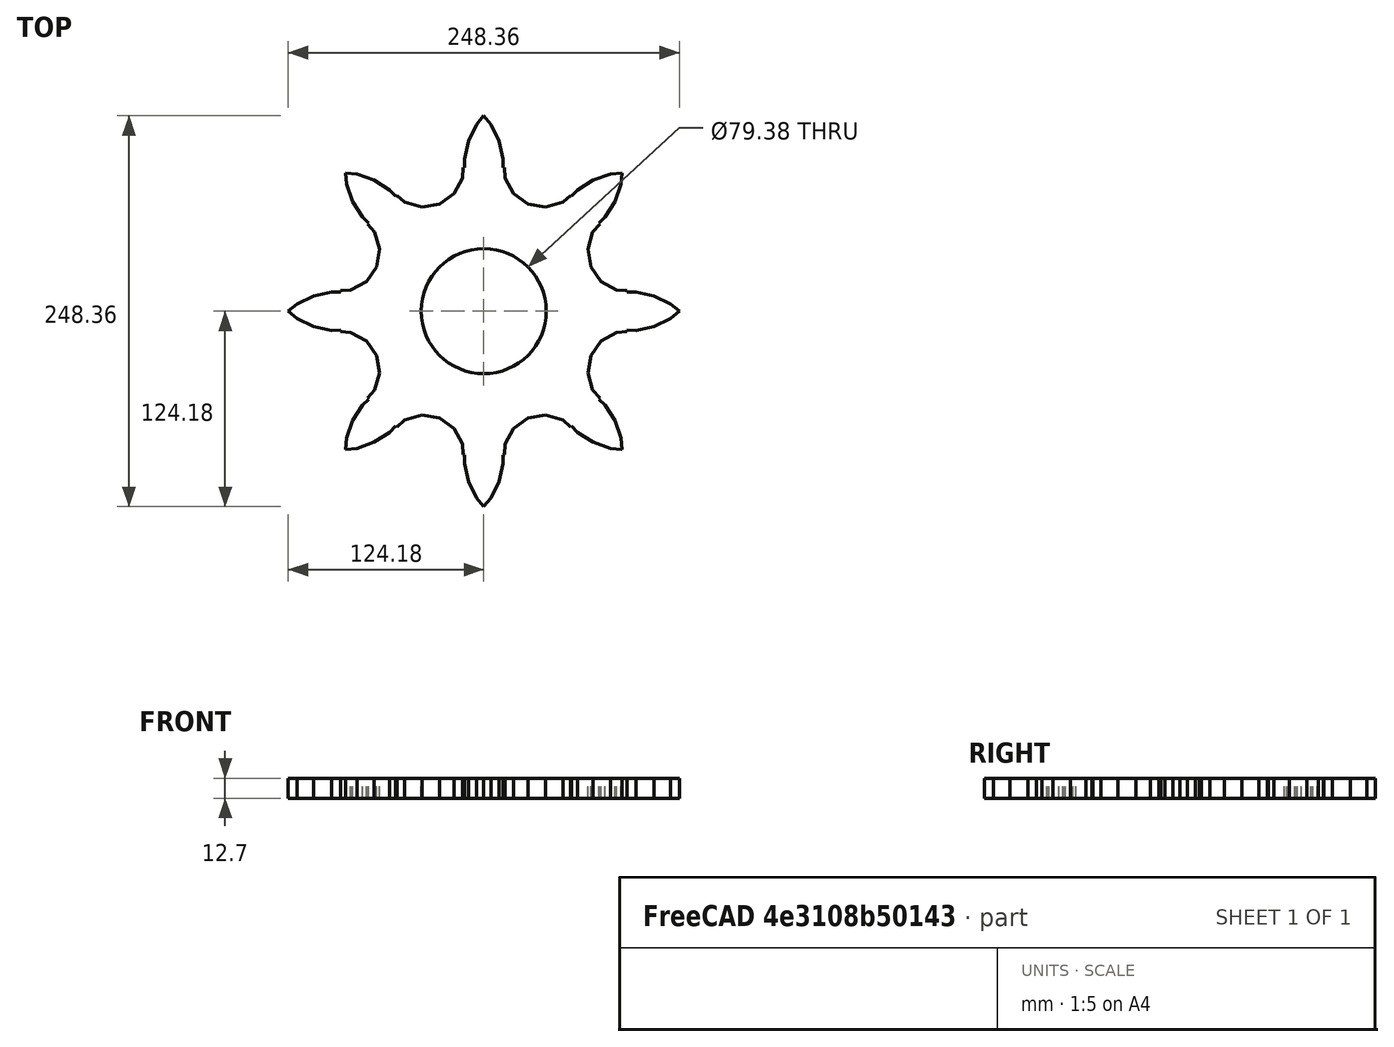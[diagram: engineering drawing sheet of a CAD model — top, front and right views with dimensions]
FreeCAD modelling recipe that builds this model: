
FCSTD DOCUMENT  (FreeCAD 0.16R6712 (Git))
Label: Sprocket
License: All rights reserved
LicenseURL: http://en.wikipedia.org/wiki/All_rights_reserved
objects: Sketcher::SketchObject×1, PartDesign::Pad×1, Part::Feature×1
note: 4 computed .brp shape members not serialized (recipe doc carries the construction recipe); baked Part::Feature solids carry a one-line shape summary decoded from their .brp

FEATURE [Sketcher::SketchObject] Sketch129
  sketch-geometry (129):
    g0: LineSegment StartX=-124.179 StartY=0 StartZ=0 EndX=-118.568 EndY=4.57225 EndZ=0
    g1: LineSegment StartX=-90.9735 StartY=13.09 StartZ=0 EndX=-84.4613 EndY=13.4541 EndZ=0
    g2: LineSegment StartX=-28.1677 StartY=67.9988 StartZ=0 EndX=-18.9337 EndY=74.5528 EndZ=0
    g3: LineSegment StartX=-66.1067 StartY=39.3297 StartZ=0 EndX=-69.2404 EndY=50.2112 EndZ=0
    g4: LineSegment StartX=-18.9337 StartY=74.5528 StartZ=0 EndX=-13.4541 EndY=84.4613 EndZ=0
    g5: LineSegment StartX=4.57225 StartY=118.568 StartZ=0 EndX=9.66978 EndY=108.045 EndZ=0
    g6: LineSegment StartX=55.8281 StartY=72.9651 StartZ=0 EndX=59.696 EndY=76.9523 EndZ=0
    g7: LineSegment StartX=-12.2006 StartY=96.6262 StartZ=0 EndX=-9.66978 EndY=108.045 EndZ=0
    g8: LineSegment StartX=12.2006 StartY=96.6262 StartZ=0 EndX=12.123 EndY=91.3197 EndZ=0
    g9: LineSegment StartX=76.9523 StartY=59.696 StartZ=0 EndX=73.1561 EndY=56.0131 EndZ=0
    g10: LineSegment StartX=83.2317 StartY=69.5568 StartZ=0 EndX=76.9523 EndY=59.696 EndZ=0
    g11: LineSegment StartX=-80.6054 StartY=87.0758 StartZ=0 EndX=-69.5568 EndY=83.2317 EndZ=0
    g12: LineSegment StartX=13.084 StartY=91.1168 StartZ=0 EndX=13.4541 EndY=84.4613 EndZ=0
    g13: LineSegment StartX=-74.5528 StartY=18.9337 StartZ=0 EndX=-67.9988 EndY=28.1677 EndZ=0
    g14: LineSegment StartX=12.123 StartY=91.3197 StartZ=0 EndX=13.084 EndY=91.1168 EndZ=0
    g15: LineSegment StartX=0 StartY=124.179 StartZ=0 EndX=4.57225 EndY=118.568 EndZ=0
    g16: LineSegment StartX=84.4613 StartY=13.4541 StartZ=0 EndX=90.9735 EndY=13.09 EndZ=0
    g17: LineSegment StartX=90.9735 StartY=13.09 StartZ=0 EndX=91.075 EndY=12.1171 EndZ=0
    g18: LineSegment StartX=96.6262 StartY=12.2006 StartZ=0 EndX=108.045 EndY=9.66978 EndZ=0
    g19: LineSegment StartX=91.075 StartY=12.1171 StartZ=0 EndX=96.6262 EndY=12.2006 EndZ=0
    g20: LineSegment StartX=118.568 StartY=4.57225 StartZ=0 EndX=124.179 EndY=0 EndZ=0
    g21: LineSegment StartX=-55.8281 StartY=72.9651 StartZ=0 EndX=-55.0282 EndY=73.544 EndZ=0
    g22: LineSegment StartX=-13.084 StartY=91.1168 StartZ=0 EndX=-12.123 EndY=91.3197 EndZ=0
    g23: LineSegment StartX=-55.0282 StartY=73.544 StartZ=0 EndX=-50.2112 EndY=69.2404 EndZ=0
    g24: LineSegment StartX=-96.6262 StartY=12.2006 StartZ=0 EndX=-91.075 EndY=12.1171 EndZ=0
    g25: LineSegment StartX=50.2112 StartY=69.2404 StartZ=0 EndX=55.0282 EndY=73.544 EndZ=0
    g26: LineSegment StartX=13.4541 StartY=84.4613 StartZ=0 EndX=18.9337 EndY=74.5528 EndZ=0
    g27: LineSegment StartX=39.3297 StartY=66.1067 StartZ=0 EndX=50.2112 EndY=69.2404 EndZ=0
    g28: LineSegment StartX=18.9337 StartY=74.5528 StartZ=0 EndX=28.1677 EndY=67.9988 EndZ=0
    g29: LineSegment StartX=28.1677 StartY=67.9988 StartZ=0 EndX=39.3297 EndY=66.1067 EndZ=0
    g30: LineSegment StartX=-87.81 StartY=87.81 StartZ=0 EndX=-80.6054 EndY=87.0758 EndZ=0
    g31: LineSegment StartX=-108.045 StartY=9.66978 StartZ=0 EndX=-96.6262 EndY=12.2006 EndZ=0
    g32: LineSegment StartX=-4.57225 StartY=118.568 StartZ=0 EndX=0 EndY=124.179 EndZ=0
    g33: LineSegment StartX=9.66978 StartY=108.045 StartZ=0 EndX=12.2006 EndY=96.6262 EndZ=0
    g34: LineSegment StartX=-13.4541 StartY=84.4613 StartZ=0 EndX=-13.084 EndY=91.1168 EndZ=0
    g35: LineSegment StartX=-118.568 StartY=4.57225 StartZ=0 EndX=-108.045 EndY=9.66978 EndZ=0
    g36: LineSegment StartX=-83.2317 StartY=69.5568 StartZ=0 EndX=-87.0758 EndY=80.6054 EndZ=0
    g37: LineSegment StartX=73.1561 StartY=56.0131 StartZ=0 EndX=73.7947 EndY=55.3028 EndZ=0
    g38: LineSegment StartX=73.7947 StartY=55.3028 StartZ=0 EndX=69.2404 EndY=50.2112 EndZ=0
    g39: LineSegment StartX=-76.9523 StartY=59.696 StartZ=0 EndX=-83.2317 EndY=69.5568 EndZ=0
    g40: LineSegment StartX=-91.075 StartY=12.1171 StartZ=0 EndX=-90.9735 EndY=13.09 EndZ=0
    g41: LineSegment StartX=59.696 StartY=76.9523 StartZ=0 EndX=69.5568 EndY=83.2317 EndZ=0
    g42: LineSegment StartX=69.5568 StartY=83.2317 StartZ=0 EndX=80.6054 EndY=87.0758 EndZ=0
    g43: LineSegment StartX=80.6054 StartY=87.0758 StartZ=0 EndX=87.81 EndY=87.81 EndZ=0
    g44: LineSegment StartX=-39.3297 StartY=66.1067 StartZ=0 EndX=-28.1677 EndY=67.9988 EndZ=0
    g45: LineSegment StartX=55.0282 StartY=73.544 StartZ=0 EndX=55.8281 EndY=72.9651 EndZ=0
    g46: LineSegment StartX=-84.4613 StartY=13.4541 StartZ=0 EndX=-74.5528 EndY=18.9337 EndZ=0
    g47: LineSegment StartX=-59.696 StartY=76.9523 StartZ=0 EndX=-55.8281 EndY=72.9651 EndZ=0
    g48: LineSegment StartX=87.81 StartY=87.81 StartZ=0 EndX=87.0758 EndY=80.6054 EndZ=0
    g49: LineSegment StartX=87.0758 StartY=80.6054 StartZ=0 EndX=83.2317 EndY=69.5568 EndZ=0
    g50: LineSegment StartX=-9.66978 StartY=108.045 StartZ=0 EndX=-4.57225 EndY=118.568 EndZ=0
    g51: LineSegment StartX=-87.0758 StartY=80.6054 StartZ=0 EndX=-87.81 EndY=87.81 EndZ=0
    g52: LineSegment StartX=-12.123 StartY=91.3197 StartZ=0 EndX=-12.2006 EndY=96.6262 EndZ=0
    g53: LineSegment StartX=91.075 StartY=-12.1171 StartZ=0 EndX=90.9735 EndY=-13.09 EndZ=0
    g54: LineSegment StartX=108.045 StartY=9.66978 StartZ=0 EndX=118.568 EndY=4.57225 EndZ=0
    g55: LineSegment StartX=118.568 StartY=-4.57225 StartZ=0 EndX=108.045 EndY=-9.66978 EndZ=0
    g56: LineSegment StartX=124.179 StartY=0 StartZ=0 EndX=118.568 EndY=-4.57225 EndZ=0
    g57: LineSegment StartX=108.045 StartY=-9.66978 StartZ=0 EndX=96.6262 EndY=-12.2006 EndZ=0
    g58: LineSegment StartX=-73.7947 StartY=55.3028 StartZ=0 EndX=-73.1561 EndY=56.0131 EndZ=0
    g59: LineSegment StartX=69.2404 StartY=50.2112 StartZ=0 EndX=66.1067 EndY=39.3297 EndZ=0
    g60: LineSegment StartX=66.1067 StartY=39.3297 StartZ=0 EndX=67.9988 EndY=28.1677 EndZ=0
    g61: LineSegment StartX=67.9988 StartY=28.1677 StartZ=0 EndX=74.5528 EndY=18.9337 EndZ=0
    g62: LineSegment StartX=74.5528 StartY=18.9337 StartZ=0 EndX=84.4613 EndY=13.4541 EndZ=0
    g63: LineSegment StartX=-50.2112 StartY=69.2404 StartZ=0 EndX=-39.3297 EndY=66.1067 EndZ=0
    g64: LineSegment StartX=-67.9988 StartY=28.1677 StartZ=0 EndX=-66.1067 EndY=39.3297 EndZ=0
    g65: LineSegment StartX=-69.2404 StartY=50.2112 StartZ=0 EndX=-73.7947 EndY=55.3028 EndZ=0
    g66: LineSegment StartX=-69.5568 StartY=83.2317 StartZ=0 EndX=-59.696 EndY=76.9523 EndZ=0
    g67: LineSegment StartX=96.6262 StartY=-12.2006 StartZ=0 EndX=91.075 EndY=-12.1171 EndZ=0
    g68: LineSegment StartX=67.9988 StartY=-28.1677 StartZ=0 EndX=66.1067 EndY=-39.3297 EndZ=0
    g69: LineSegment StartX=90.9735 StartY=-13.09 StartZ=0 EndX=84.4613 EndY=-13.4541 EndZ=0
    g70: LineSegment StartX=84.4613 StartY=-13.4541 StartZ=0 EndX=74.5528 EndY=-18.9337 EndZ=0
    g71: LineSegment StartX=66.1067 StartY=-39.3297 StartZ=0 EndX=69.2404 EndY=-50.2112 EndZ=0
    g72: LineSegment StartX=74.5528 StartY=-18.9337 StartZ=0 EndX=67.9988 EndY=-28.1677 EndZ=0
    g73: LineSegment StartX=-73.1561 StartY=56.0131 StartZ=0 EndX=-76.9523 EndY=59.696 EndZ=0
    g74: LineSegment StartX=69.2404 StartY=-50.2112 StartZ=0 EndX=73.7947 EndY=-55.3028 EndZ=0
    g75: LineSegment StartX=73.7947 StartY=-55.3028 StartZ=0 EndX=73.1561 EndY=-56.0131 EndZ=0
    g76: LineSegment StartX=73.1561 StartY=-56.0131 StartZ=0 EndX=76.9523 EndY=-59.696 EndZ=0
    g77: LineSegment StartX=83.2317 StartY=-69.5568 StartZ=0 EndX=87.0758 EndY=-80.6054 EndZ=0
    g78: LineSegment StartX=87.0758 StartY=-80.6054 StartZ=0 EndX=87.81 EndY=-87.81 EndZ=0
    g79: LineSegment StartX=76.9523 StartY=-59.696 StartZ=0 EndX=83.2317 EndY=-69.5568 EndZ=0
    g80: LineSegment StartX=87.81 StartY=-87.81 StartZ=0 EndX=80.6054 EndY=-87.0758 EndZ=0
    g81: LineSegment StartX=80.6054 StartY=-87.0758 StartZ=0 EndX=69.5568 EndY=-83.2317 EndZ=0
    g82: LineSegment StartX=69.5568 StartY=-83.2317 StartZ=0 EndX=59.696 EndY=-76.9523 EndZ=0
    g83: LineSegment StartX=59.696 StartY=-76.9523 StartZ=0 EndX=55.8281 EndY=-72.9651 EndZ=0
    g84: LineSegment StartX=50.2112 StartY=-69.2404 StartZ=0 EndX=39.3297 EndY=-66.1067 EndZ=0
    g85: LineSegment StartX=55.8281 StartY=-72.9651 StartZ=0 EndX=55.0282 EndY=-73.544 EndZ=0
    g86: LineSegment StartX=55.0282 StartY=-73.544 StartZ=0 EndX=50.2112 EndY=-69.2404 EndZ=0
    g87: LineSegment StartX=39.3297 StartY=-66.1067 StartZ=0 EndX=28.1677 EndY=-67.9988 EndZ=0
    g88: LineSegment StartX=28.1677 StartY=-67.9988 StartZ=0 EndX=18.9337 EndY=-74.5528 EndZ=0
    g89: LineSegment StartX=13.4541 StartY=-84.4613 StartZ=0 EndX=13.084 EndY=-91.1168 EndZ=0
    g90: LineSegment StartX=18.9337 StartY=-74.5528 StartZ=0 EndX=13.4541 EndY=-84.4613 EndZ=0
    g91: LineSegment StartX=13.084 StartY=-91.1168 StartZ=0 EndX=12.123 EndY=-91.3197 EndZ=0
    g92: LineSegment StartX=12.123 StartY=-91.3197 StartZ=0 EndX=12.2006 EndY=-96.6262 EndZ=0
    g93: LineSegment StartX=12.2006 StartY=-96.6262 StartZ=0 EndX=9.66978 EndY=-108.045 EndZ=0
    g94: LineSegment StartX=9.66978 StartY=-108.045 StartZ=0 EndX=4.57225 EndY=-118.568 EndZ=0
    g95: LineSegment StartX=4.57225 StartY=-118.568 StartZ=0 EndX=0 EndY=-124.179 EndZ=0
    g96: LineSegment StartX=-9.66978 StartY=-108.045 StartZ=0 EndX=-12.2006 EndY=-96.6262 EndZ=0
    g97: LineSegment StartX=0 StartY=-124.179 StartZ=0 EndX=-4.57225 EndY=-118.568 EndZ=0
    g98: LineSegment StartX=-4.57225 StartY=-118.568 StartZ=0 EndX=-9.66978 EndY=-108.045 EndZ=0
    g99: LineSegment StartX=-12.2006 StartY=-96.6262 StartZ=0 EndX=-12.123 EndY=-91.3197 EndZ=0
    g100: LineSegment StartX=-12.123 StartY=-91.3197 StartZ=0 EndX=-13.084 EndY=-91.1168 EndZ=0
    g101: LineSegment StartX=-13.084 StartY=-91.1168 StartZ=0 EndX=-13.4541 EndY=-84.4613 EndZ=0
    g102: LineSegment StartX=-13.4541 StartY=-84.4613 StartZ=0 EndX=-18.9337 EndY=-74.5528 EndZ=0
    g103: LineSegment StartX=-18.9337 StartY=-74.5528 StartZ=0 EndX=-28.1677 EndY=-67.9988 EndZ=0
    g104: LineSegment StartX=-28.1677 StartY=-67.9988 StartZ=0 EndX=-39.3297 EndY=-66.1067 EndZ=0
    g105: LineSegment StartX=-39.3297 StartY=-66.1067 StartZ=0 EndX=-50.2112 EndY=-69.2404 EndZ=0
    g106: LineSegment StartX=-50.2112 StartY=-69.2404 StartZ=0 EndX=-55.0282 EndY=-73.544 EndZ=0
    g107: LineSegment StartX=-55.0282 StartY=-73.544 StartZ=0 EndX=-55.8281 EndY=-72.9651 EndZ=0
    g108: LineSegment StartX=-55.8281 StartY=-72.9651 StartZ=0 EndX=-59.696 EndY=-76.9523 EndZ=0
    g109: LineSegment StartX=-69.5568 StartY=-83.2317 StartZ=0 EndX=-80.6054 EndY=-87.0758 EndZ=0
    g110: LineSegment StartX=-59.696 StartY=-76.9523 StartZ=0 EndX=-69.5568 EndY=-83.2317 EndZ=0
    g111: LineSegment StartX=-80.6054 StartY=-87.0758 StartZ=0 EndX=-87.81 EndY=-87.81 EndZ=0
    g112: LineSegment StartX=-87.0758 StartY=-80.6054 StartZ=0 EndX=-83.2317 EndY=-69.5568 EndZ=0
    g113: LineSegment StartX=-87.81 StartY=-87.81 StartZ=0 EndX=-87.0758 EndY=-80.6054 EndZ=0
    g114: LineSegment StartX=-83.2317 StartY=-69.5568 StartZ=0 EndX=-76.9523 EndY=-59.696 EndZ=0
    g115: LineSegment StartX=-73.1561 StartY=-56.0131 StartZ=0 EndX=-73.7947 EndY=-55.3028 EndZ=0
    g116: LineSegment StartX=-76.9523 StartY=-59.696 StartZ=0 EndX=-73.1561 EndY=-56.0131 EndZ=0
    g117: LineSegment StartX=-73.7947 StartY=-55.3028 StartZ=0 EndX=-69.2404 EndY=-50.2112 EndZ=0
    g118: LineSegment StartX=-66.1067 StartY=-39.3297 StartZ=0 EndX=-67.9988 EndY=-28.1677 EndZ=0
    g119: LineSegment StartX=-69.2404 StartY=-50.2112 StartZ=0 EndX=-66.1067 EndY=-39.3297 EndZ=0
    g120: LineSegment StartX=-67.9988 StartY=-28.1677 StartZ=0 EndX=-74.5528 EndY=-18.9337 EndZ=0
    g121: LineSegment StartX=-74.5528 StartY=-18.9337 StartZ=0 EndX=-84.4613 EndY=-13.4541 EndZ=0
    g122: LineSegment StartX=-84.4613 StartY=-13.4541 StartZ=0 EndX=-90.9735 EndY=-13.09 EndZ=0
    g123: LineSegment StartX=-90.9735 StartY=-13.09 StartZ=0 EndX=-91.075 EndY=-12.1171 EndZ=0
    g124: LineSegment StartX=-91.075 StartY=-12.1171 StartZ=0 EndX=-96.6262 EndY=-12.2006 EndZ=0
    g125: LineSegment StartX=-96.6262 StartY=-12.2006 StartZ=0 EndX=-108.045 EndY=-9.66978 EndZ=0
    g126: LineSegment StartX=-108.045 StartY=-9.66978 StartZ=0 EndX=-118.568 EndY=-4.57225 EndZ=0
    g127: Circle CenterX=0 CenterY=0 CenterZ=0 NormalX=0 NormalY=0 NormalZ=-1 Radius=39.6875
    g128: LineSegment StartX=-118.568 StartY=-4.57225 StartZ=0 EndX=-124.179 EndY=0 EndZ=0
FEATURE [PartDesign::Pad] Pad
  Length = 12.7
  Length2 = 100
  Sketch = -> Sketch129
  Type = 0
FEATURE [Part::Feature] Pad001
  shape: bbox 248.4 x 248.4 x 12.7 mm, 131 faces (baked)
